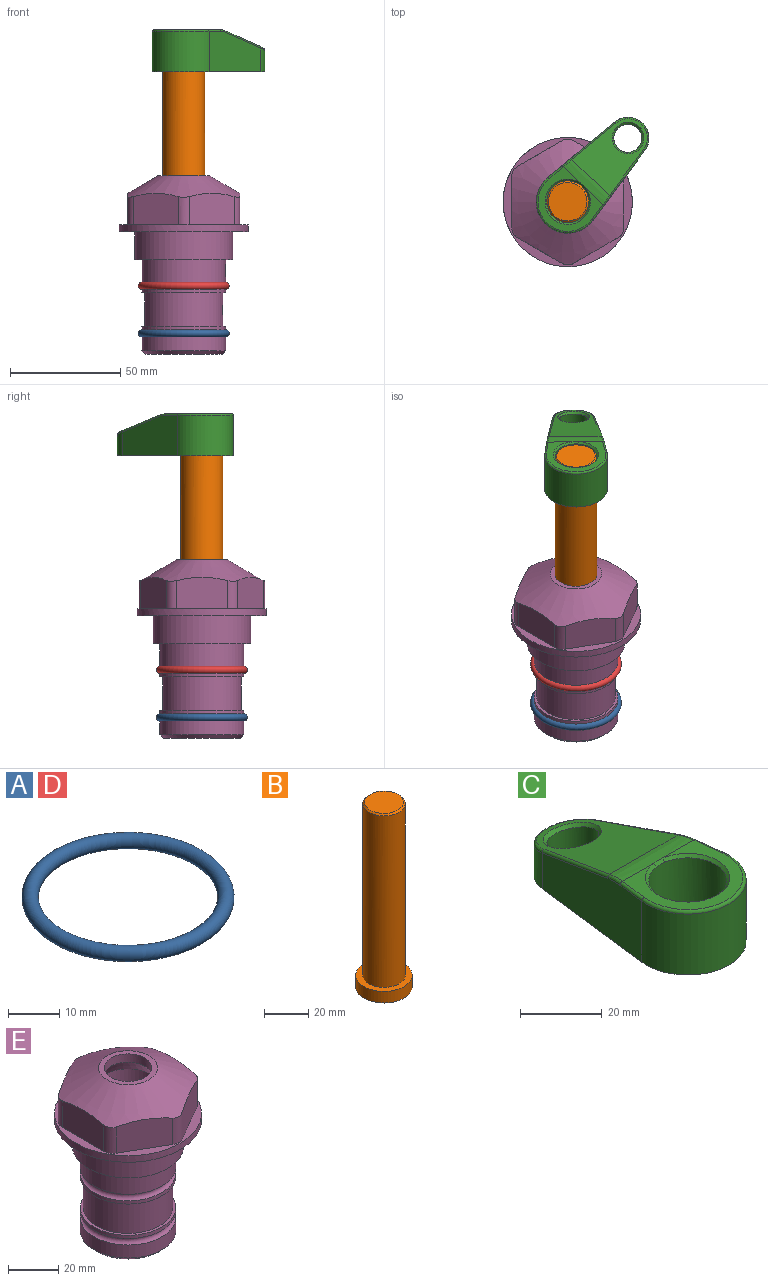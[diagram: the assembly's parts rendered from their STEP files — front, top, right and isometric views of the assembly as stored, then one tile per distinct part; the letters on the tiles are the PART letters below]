
ASSEMBLY  parts=5 mates=4
PART A: 1 faces, bbox 44.7x44.7x3.2 mm
  f0: torus R=19.05mm, axis (0,0,1), area 1193.9mm2
PART B: 6 faces, bbox 25.4x25.4x101.6 mm
  f0: plane 17.46x17.46mm, normal (0,0,1), area 239.5mm2, adj f5
  f1: plane 25.4x25.4mm, normal (0,0,-1), area 506.7mm2, adj f2
  f2: cylinder r=12.7mm len=25.4mm, axis (0,0,1), area 506.7mm2, adj f1,f3
  f3: plane 25.4x25.4mm, normal (0,0,1), area 221.7mm2, adj f2,f4
  f4: cylinder r=9.53mm len=94.46mm, axis (0,0,1), area 5653mm2, adj f3,f5
  f5: cone r=8.73mm half-angle=45deg, axis (0,0,-1), area 64.4mm2, adj f0,f4
PART C: 31 faces, bbox 31.7x65.5x19.8 mm
  f0: plane 39.12x18.26mm, normal (0.99,0.12,0), area 612.2mm2, adj f1,f4,f7,f11,f13,f15
  f1: cylinder r=9.53mm len=18.91mm, axis (0,0,-1), area 296.1mm2, adj f0,f2,f7,f17
  f2: plane 39.12x18.26mm, normal (-0.99,0.12,0), area 612.2mm2, adj f1,f4,f7,f12,f14,f16
  f3: cylinder r=6.35mm len=12.7mm, axis (0,0,-1), area 362.4mm2, adj f7,f18
  f4: cylinder r=14.29mm len=28.58mm, axis (0,0,-1), area 882.2mm2, adj f0,f2,f7,f10
  f5: cylinder r=9.53mm len=19.05mm, axis (0,0,-1), area 1092.6mm2, adj f7,f19,f20
  f6: plane 26.99x23.69mm, normal (0,0,1), area 216.2mm2, adj f9,f10,f11,f12,f19
  f7: plane 63.5x28.58mm, normal (0,0,-1), area 661.8mm2, adj f0,f1,f2,f3,f4,f5,f22,f23
  f8: plane 33.52x23.6mm, normal (0,0.26,0.97), area 486mm2, adj f9,f15,f16,f17,f18
  f9: cylinder r=19.05mm len=24.72mm, axis (1,0,0), area 120.4mm2, adj f6,f8,f13,f14,f20
  f10: torus R=13.49mm, axis (0,0,1), area 59mm2, adj f4,f6,f11,f12
  f11: cylinder r=0.79mm len=8.67mm, axis (0.12,-0.99,0), area 10.8mm2, adj f0,f6,f10,f13
  f12: cylinder r=0.79mm len=8.67mm, axis (0.12,0.99,0), area 10.8mm2, adj f2,f6,f10,f14
  f13: bspline ~4.95x1.42mm, area 6.1mm2, adj f0,f9,f11,f15
  f14: bspline ~4.95x1.42mm, area 6.1mm2, adj f2,f9,f12,f16
  f15: cylinder r=0.79mm len=25.95mm, axis (0.12,-0.96,0.26), area 32.9mm2, adj f0,f8,f13,f17
  f16: cylinder r=0.79mm len=25.95mm, axis (0.12,0.96,-0.26), area 32.9mm2, adj f2,f8,f14,f17
  f17: bspline ~18.91x8.38mm, area 30mm2, adj f1,f8,f15,f16
  f18: bspline ~14.29x14.29mm, area 48.3mm2, adj f3,f8
  f19: cone r=9.53mm half-angle=45deg, axis (0,0,1), area 66.5mm2, adj f5,f6,f20
  f20: bspline ~3.22x0.96mm, area 3.5mm2, adj f5,f9,f19
  f21: plane 2.75x2.72mm, normal (0,0,-1), area 2.9mm2, adj f23,f25,f28
  f22: plane 23.05x15.88mm, normal (-0.99,-0.12,0), area 323.6mm2, adj f7,f25,f26,f27,f28,f29
  f23: plane 23.05x15.88mm, normal (0.99,-0.12,0), area 323.6mm2, adj f7,f21,f25,f27,f28,f30
  f24: cylinder r=9.53mm len=10.69mm, axis (0,0,-1), area 114.7mm2, adj f7,f27,f29,f30
  f25: cylinder r=12.7mm len=20.59mm, axis (0,0,-1), area 381.1mm2, adj f7,f21,f22,f23,f26,f28
  f26: plane 2.75x2.72mm, normal (0,0,-1), area 2.9mm2, adj f22,f25,f28
  f27: plane 19.72x18.37mm, normal (0,-0.26,-0.97), area 291.8mm2, adj f22,f23,f24,f28,f29,f30
  f28: cylinder r=15.88mm len=19.92mm, axis (1,0,0), area 54.8mm2, adj f21,f22,f23,f25,f26,f27
  f29: cylinder r=1.59mm len=11mm, axis (0,0,-1), area 34.7mm2, adj f7,f22,f24,f27
  f30: cylinder r=1.59mm len=11mm, axis (0,0,-1), area 34.7mm2, adj f7,f23,f24,f27
PART D: same geometry as A
PART E: 36 faces, bbox 58.7x58.7x81 mm
  f0: cylinder r=17.78mm len=35.56mm, axis (0,0,1), area 1670.8mm2, adj f23,f24,f31
  f1: cylinder r=19.05mm len=38.1mm, axis (0,0,1), area 1191.9mm2, adj f26,f27,f30
  f2: plane 58.66x58.66mm, normal (0,0,-1), area 1150.6mm2, adj f3,f28
  f3: cylinder r=29.33mm len=58.66mm, axis (0,0,-1), area 585.1mm2, adj f2,f4
  f4: plane 58.66x58.66mm, normal (0,0,1), area 475.9mm2, adj f3,f5,f6,f7,f8,f9,f10,f11
  f5: plane 20.32x14.34mm, normal (-0.5,0.87,0), area 324.4mm2, adj f4,f15,f16,f17
  f6: plane 20.32x14.34mm, normal (0.5,0.87,0), area 324.4mm2, adj f4,f14,f15,f17
  f7: plane 23.48x14.34mm, normal (1,0,0), area 324.4mm2, adj f4,f13,f14,f17
  f8: plane 20.32x14.34mm, normal (0.5,-0.87,0), area 324.4mm2, adj f4,f12,f13,f17
  f9: plane 20.32x14.34mm, normal (-0.5,-0.87,0), area 324.4mm2, adj f4,f11,f12,f17
  f10: plane 23.48x14.34mm, normal (-1,0,0), area 324.4mm2, adj f4,f11,f16,f17
  f11: cylinder r=5.08mm len=12.85mm, axis (0,0,-1), area 67.2mm2, adj f4,f9,f10,f17
  f12: cylinder r=5.08mm len=12.85mm, axis (0,0,-1), area 67.2mm2, adj f4,f8,f9,f17
  f13: cylinder r=5.08mm len=12.85mm, axis (0,0,-1), area 67.2mm2, adj f4,f7,f8,f17
  f14: cylinder r=5.08mm len=12.85mm, axis (0,0,-1), area 67.2mm2, adj f4,f6,f7,f17
  f15: cylinder r=5.08mm len=12.85mm, axis (0,0,-1), area 67.2mm2, adj f4,f5,f6,f17
  f16: cylinder r=5.08mm len=12.85mm, axis (0,0,-1), area 67.2mm2, adj f4,f5,f10,f17
  f17: cone r=11.73mm half-angle=60deg, axis (0,0,-1), area 2071.8mm2, adj f5,f6,f7,f8,f9,f10,f11,f12
  f18: plane 23.46x23.46mm, normal (0,0,1), area 147.4mm2, adj f17,f35
  f19: plane 34.93x34.93mm, normal (0,0,-1), area 958mm2, adj f29
  f20: cylinder r=19.05mm len=38.1mm, axis (0,0,1), area 760.1mm2, adj f21,f29
  f21: torus R=19.05mm, axis (0,0,1), area 565.3mm2, adj f20,f22
  f22: cylinder r=19.05mm len=38.1mm, axis (0,0,1), area 190mm2, adj f21,f23
  f23: plane 38.1x38.1mm, normal (0,0,1), area 146.9mm2, adj f0,f22
  f24: plane 38.1x38.1mm, normal (0,0,-1), area 146.9mm2, adj f0,f25
  f25: cylinder r=19.05mm len=38.1mm, axis (0,0,1), area 190mm2, adj f24,f26
  f26: torus R=19.05mm, axis (0,0,1), area 565.3mm2, adj f1,f25
  f27: plane 44.45x44.45mm, normal (0,0,-1), area 411.7mm2, adj f1,f28
  f28: cylinder r=22.23mm len=44.45mm, axis (0,0,1), area 1773.5mm2, adj f2,f27
  f29: cone r=19.05mm half-angle=45deg, axis (0,0,1), area 257.5mm2, adj f19,f20
  f30: cylinder r=3.17mm len=6.75mm, axis (-1,0,0), area 128mm2, adj f1,f33
  f31: cylinder r=3.17mm len=6.35mm, axis (-1,0,0), area 102.5mm2, adj f0,f33
  f32: plane 25.4x25.4mm, normal (0,0,1), area 506.7mm2, adj f33
  f33: cylinder r=12.7mm len=66.42mm, axis (0,0,-1), area 5236.2mm2, adj f30,f31,f32,f34
  f34: cone r=9.53mm half-angle=30deg, axis (0,0,-1), area 443.4mm2, adj f33,f35
  f35: cylinder r=9.53mm len=19.05mm, axis (0,0,-1), area 240.9mm2, adj f18,f34
PLACE A t=(0,0,-21.59)mm
PLACE B rot(axis=(0,0,-1),43.4deg) t=(0,0,27.55)mm
PLACE C rot(axis=(0,0,-1),43.4deg) t=(0,0,28.35)mm
PLACE D at identity
PLACE E at identity fixed
MATE fastened C.f4 <-> B.f2  axis (0,0,-1) through (0,0,91.05)mm
MATE cylindrical B.f2 <-> E.f0  axis (0,0,-1) through (0,0,-10.55)mm
MATE fastened D.f0 <-> E.f0  axis (0,0,1) through (0,0,-24.51)mm
MATE fastened A.f0 <-> E.f0  axis (0,0,1) through (0,0,-46.1)mm
